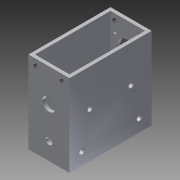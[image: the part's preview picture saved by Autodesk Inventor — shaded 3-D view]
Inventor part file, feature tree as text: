
AUTODESK INVENTOR PART (.ipt)
format: ipt  version: 2013 (Build 170138000, 138)  size: 203,776 bytes
history: native  units: mm
features: sketch x7, hole x5, thread x4, extrude x2, other x1
ambient origin geometry x1: Origin
feature tree (19):
  other  "ソリッド1"
  extrude  "押し出し1"  Depth=25.0mm
  extrude  "押し出し2"  Depth=50.0mm
  hole  "穴1"  [1 undecoded]
  hole  "穴2"  [1 undecoded]
  hole  "穴4"  [1 undecoded]
  thread  "ねじ1"
  thread  "ねじ2"
  thread  "ねじ3"
  thread  "ねじ4"
  hole  "穴5"  [1 undecoded]
  hole  "穴7"  [1 undecoded]
  sketch  "スケッチ1"
  sketch  "スケッチ2"
  sketch  "スケッチ3"
  sketch  "スケッチ4"
  sketch  "スケッチ5"
  sketch  "スケッチ7"
  sketch  "スケッチ8"
note: 5 required parameter values undecoded (feature->parameter linkage not recoverable at this tier; creation-order binding heuristic only, values carry confidence <= 0.55)
